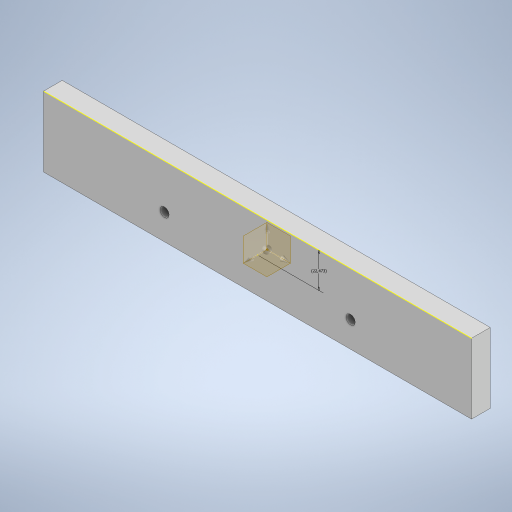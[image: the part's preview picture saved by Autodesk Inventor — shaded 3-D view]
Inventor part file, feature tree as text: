
AUTODESK INVENTOR PART (.ipt)
format: ipt  version: 2024 (Build 280153000, 153)  size: 231,424 bytes
history: native  units: mm
features: other x6, sketch x1
ambient origin geometry x8: Origin, YZ Plane, XZ Plane, XY Plane, X Axis, Y Axis, Z Axis, Center Point
bodies: Body1 (feature_tree)
feature tree (7):
  other  "BORDE_5"
  other  "Generador_de_Piezas.ipt"
  other  "Desplazar cuerpo1"
  sketch  "Boceto1"  dims[d0=10.0mm d1=-179.974mm d2=-2286.154mm d3=0.0mm d4=22.47274mm d5=0.0mm d6=-0.027mm d7=0.0mm]
  other  "Desplazar cuerpo2"
  other  "BORDE_5::Generador_de_Piezas.ipt"
  other  "OperaciónIdentificador1"
